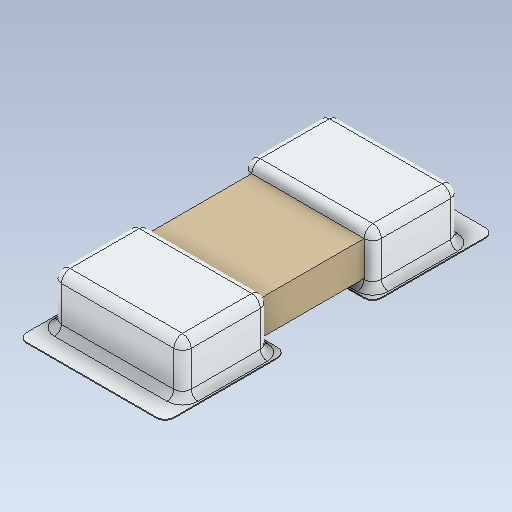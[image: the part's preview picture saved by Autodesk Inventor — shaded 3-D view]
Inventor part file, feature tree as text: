
AUTODESK INVENTOR PART (.ipt)
format: ipt  version: 2020 (Build 240168000, 168)  size: 175,616 bytes
history: native  units: in
note: dims shown in document units (in); Inventor stores cm internally (conversion verified against a paired STEP export)
features: fillet x1
ambient origin geometry x8: Origin, YZ Plane, XZ Plane, XY Plane, X Axis, Y Axis, Z Axis, Center Point
bodies: Solid1 (feature_tree)
feature tree (1):
  fillet  "Fillet2"  [1 undecoded]
note: 1 required parameter value undecoded (feature->parameter linkage not recoverable at this tier; creation-order binding heuristic only, values carry confidence <= 0.55)
